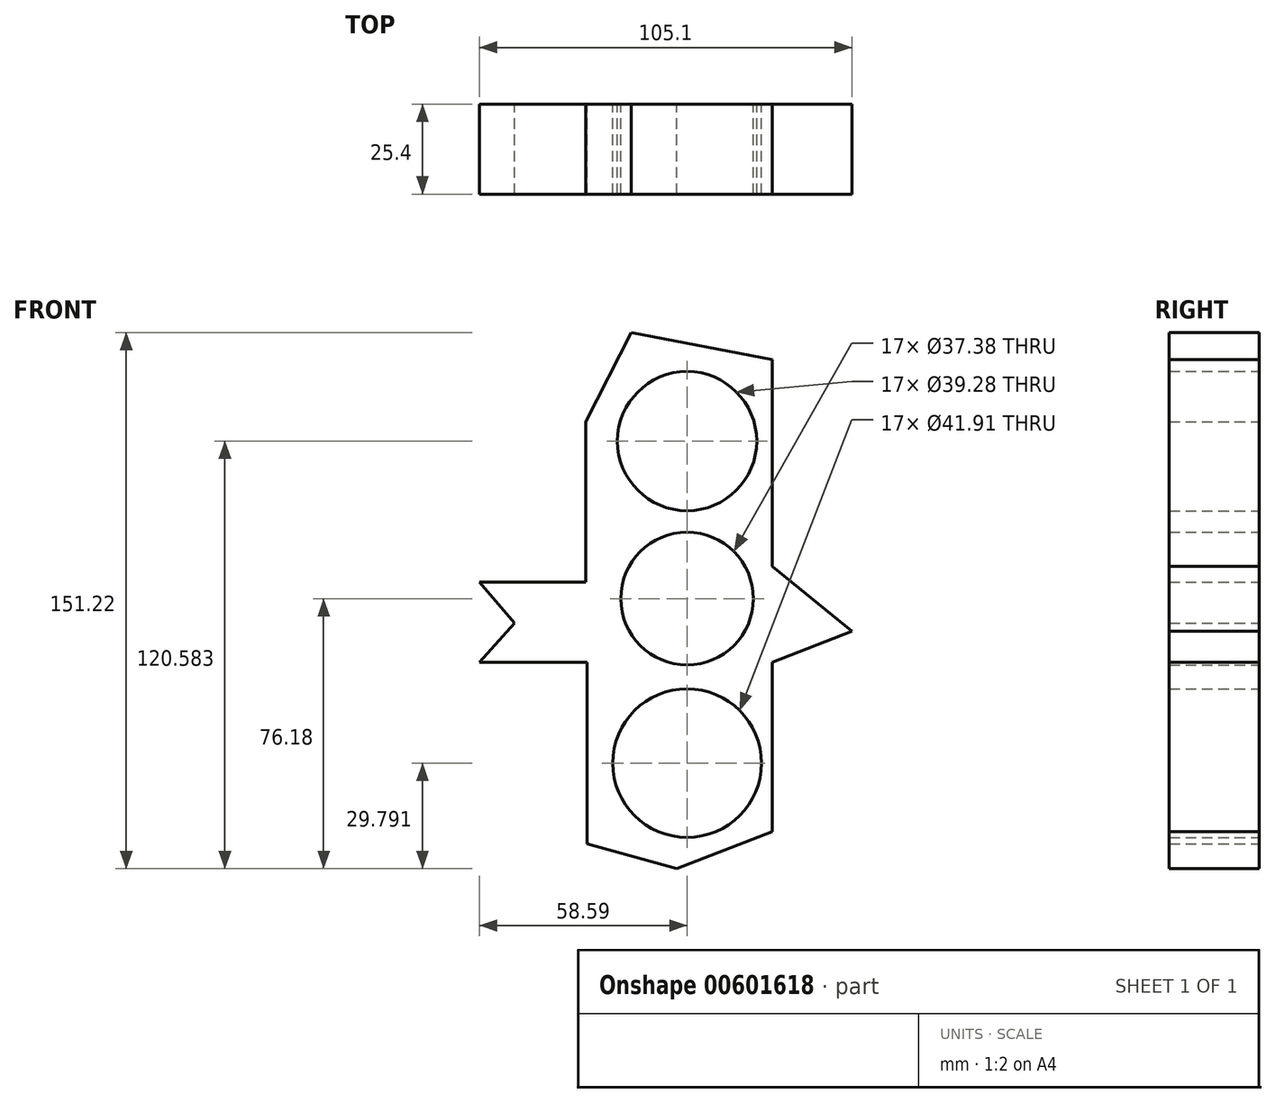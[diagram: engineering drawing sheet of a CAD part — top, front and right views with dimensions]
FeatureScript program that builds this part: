
annotation { "Feature Type Name" : "Feature", "Feature Type Description" : "" }
export const myFeature = defineFeature(function(context is Context, id is Id, definition is map)
    precondition{}
    {
        {
            var Q0;
            Q0=qCreatedBy(makeId("Front.planeOp"),FACE);
            var sketch = newSketch(context, id + "F0", { "sketchPlane" : qUnion([Q0])});
            skCircle(sketch, "E0", {"center": v(0, 0) * mm, "radius": 18.7 * mm});
            skCircle(sketch, "E1", {"center": v(0, 0) * mm, "radius": 11.32 * mm});
            skCircle(sketch, "E2", {"center": v(0, 44.4) * mm, "radius": 12.39 * mm});
            skCircle(sketch, "E3", {"center": v(0, 44.4) * mm, "radius": 19.64 * mm});
            skCircle(sketch, "E4", {"center": v(0, -46.39) * mm, "radius": 12.94 * mm});
            skCircle(sketch, "E5", {"center": v(0, -46.39) * mm, "radius": 20.96 * mm});
            skLineSegment(sketch, "E6", {"start": v(-28.51, 49.8) * mm, "end": v(-28.51, 19.44) * mm});
            skLineSegment(sketch, "E7", {"start": v(-28.51, 19.44) * mm, "end": v(-28.51, 4.68) * mm});
            skLineSegment(sketch, "E8", {"start": v(-28.51, 4.68) * mm, "end": v(-38.73, 4.68) * mm});
            skLineSegment(sketch, "E9", {"start": v(-38.73, -18.02) * mm, "end": v(-28.23, -18.02) * mm});
            skLineSegment(sketch, "E10", {"start": v(-28.23, -18.02) * mm, "end": v(-28.23, -69.09) * mm});
            skLineSegment(sketch, "E11", {"start": v(-28.23, -69.09) * mm, "end": v(-2.98, -76.18) * mm});
            skLineSegment(sketch, "E12", {"start": v(-2.98, -76.18) * mm, "end": v(23.97, -65.68) * mm});
            skLineSegment(sketch, "E13", {"start": v(23.97, -65.68) * mm, "end": v(23.97, -18.02) * mm});
            skLineSegment(sketch, "E14", {"start": v(23.97, -18.02) * mm, "end": v(46.5, -9.24) * mm});
            skLineSegment(sketch, "E15", {"start": v(46.5, -9.24) * mm, "end": v(23.97, 9.02) * mm});
            skLineSegment(sketch, "E16", {"start": v(23.97, 9.02) * mm, "end": v(23.97, 45.54) * mm});
            skLineSegment(sketch, "E17", {"start": v(23.97, 45.54) * mm, "end": v(23.97, 64.83) * mm});
            skLineSegment(sketch, "E18", {"start": v(23.97, 64.83) * mm, "end": v(23.97, 67.38) * mm});
            skLineSegment(sketch, "E19", {"start": v(23.97, 67.38) * mm, "end": v(-15.75, 75.04) * mm});
            skLineSegment(sketch, "E20", {"start": v(-15.75, 75.04) * mm, "end": v(-28.51, 49.8) * mm});
            skLineSegment(sketch, "E21", {"start": v(-38.73, -18.02) * mm, "end": v(-58.59, -18.02) * mm});
            skLineSegment(sketch, "E22", {"start": v(-38.73, 4.68) * mm, "end": v(-58.59, 4.68) * mm});
            skLineSegment(sketch, "E23", {"start": v(-58.59, -18.02) * mm, "end": v(-48.66, -6.95) * mm});
            skPoint(sketch, "E23.endSnap0", {"position": v(-48.66, -18.02) * mm});
            skLineSegment(sketch, "E24", {"start": v(-48.66, -6.95) * mm, "end": v(-58.59, 4.68) * mm});
            skSolve(sketch);
        }
        {
            var Q0;
            Q0=makeQuery(id+"F0.imprint","IMPRINT",FACE,{"disambiguationData":[TD([[makeQuery(id+"F0.imprint","IMPRINT",EDGE,{"derivedFrom":sQuery(id+"F0.wireOp",EDGE,"E0")}),-1.0]])]});
            extrude(context, id + "F1", {"entities" : qUnion([Q0]), "depth" : 25.4 * mm, "offsetDistance" : 25.4 * mm});
        }
    });
